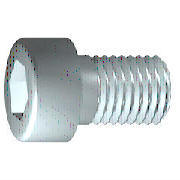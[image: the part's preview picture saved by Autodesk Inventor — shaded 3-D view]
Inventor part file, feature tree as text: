
AUTODESK INVENTOR PART (.ipt)
format: ipt  version: 2013 (Build 170138000, 138)  size: 181,248 bytes
history: native  units: mm (DEFAULTED — no unit token found)
features: sketch x2, extrude x1, plane x1, fillet x1
ambient origin geometry x7: Origin, YZ Plane, XY Plane, X Axis, Y Axis, Z Axis, Center Point
bodies: Solid1 (feature_tree), Body (feature_tree)
feature tree (5):
  extrude  "Slot"  Depth=0.306825mm
  plane  "Work Plane1"
  fillet  "Fillet2"  Radius=3.0mm
  sketch  "Sketch1"  dims[d1=18.0mm d2=0.306825mm d3=3.0mm]
  sketch  "Sketch2"  dims[d4=1.5mm d5=60.0deg d6=3.0mm d7=3.0mm d8=2.886751mm d9=5.5mm d10=90.0deg d11=10.0mm d12=0.0mm d13=18.0mm d14=0.0mm d15=0.306725mm d16=0.306725mm d17=0.3mm d19=0.0mm d26=35.0mm d27=45.0deg d28=0.0mm d29=0.0mm d30=0.1mm]
